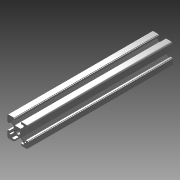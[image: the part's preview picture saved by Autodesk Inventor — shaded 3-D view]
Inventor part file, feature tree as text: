
AUTODESK INVENTOR PART (.ipt)
format: ipt  version: 2015 SP1 (Build 190203100, 203)  size: 155,136 bytes
history: native  units: mm
features: extrude x2, mirror x2, sketch x2, fillet x1
ambient origin geometry x8: Origin, YZ Plane, XZ Plane, XY Plane, X Axis, Y Axis, Z Axis, Center Point
bodies: Solid1 (feature_tree)
feature tree (7):
  extrude  "Extrusion1"  Depth=10.0mm
  fillet  "Fillet1"  Radius=10.0mm
  mirror  "Mirror1"
  mirror  "Mirror2"
  extrude  "Extrusion2"  Depth=6.1mm
  sketch  "Sketch1"  dims[d0=45.0deg d1=5.63mm d2=10.0mm]
  sketch  "Sketch2"  dims[d3=3.1mm d5=6.1mm d6=1.5mm d7=2.0mm d8=140.0mm d9=0.0mm d10=1.5mm d11=3.6mm d12=4.45mm d13=10.0mm d14=0.0mm]
